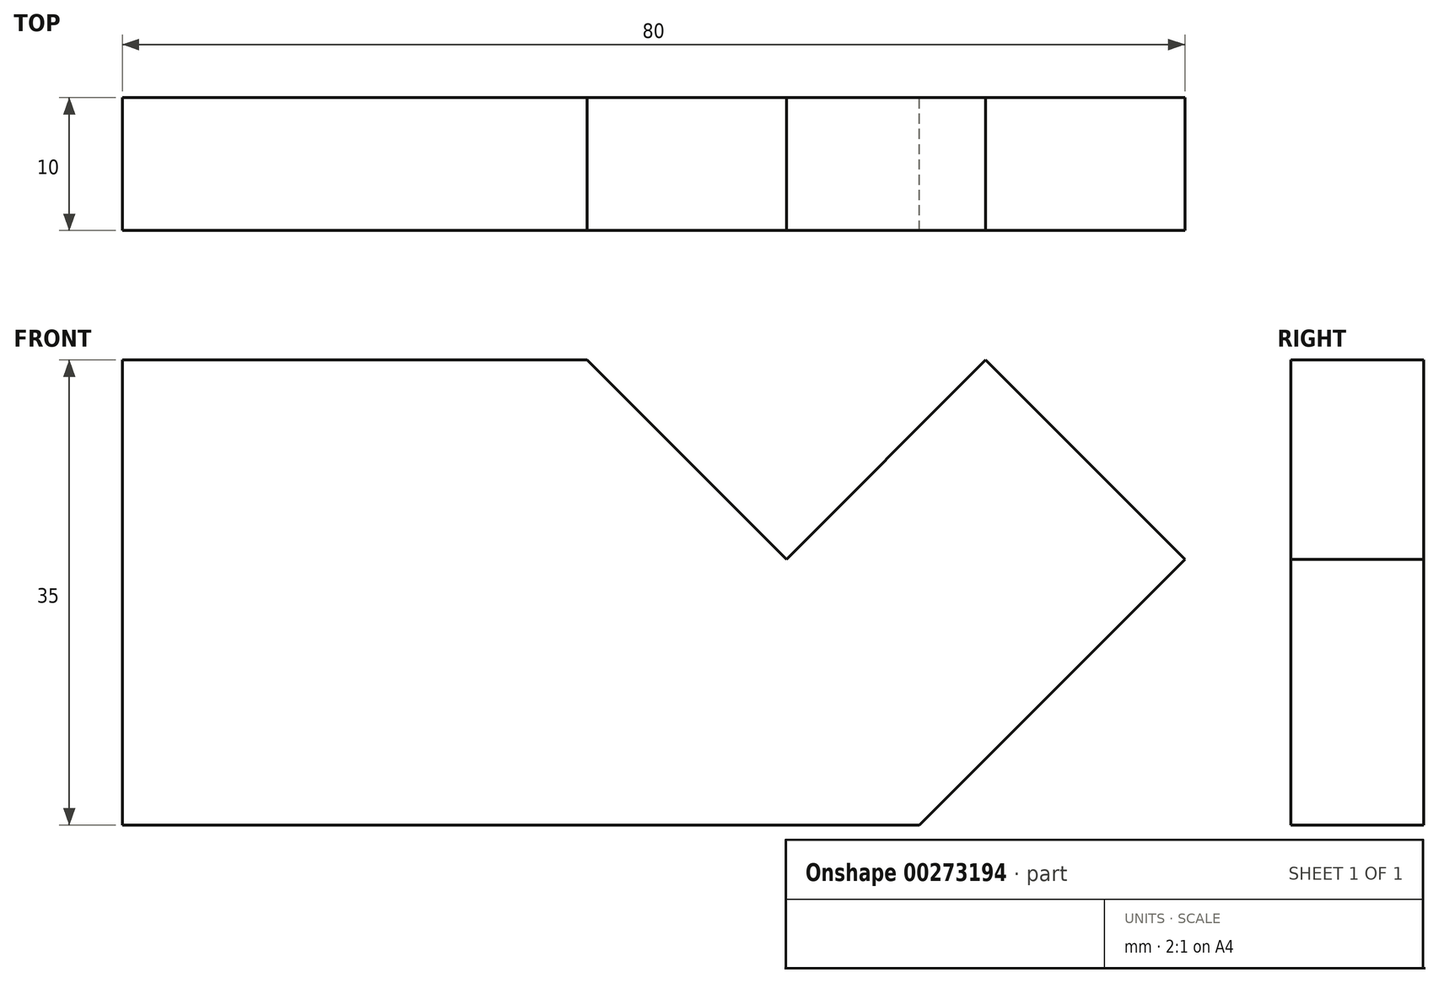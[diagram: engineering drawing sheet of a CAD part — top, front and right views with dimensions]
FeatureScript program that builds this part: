
annotation { "Feature Type Name" : "Feature", "Feature Type Description" : "" }
export const myFeature = defineFeature(function(context is Context, id is Id, definition is map)
    precondition{}
    {
        {
            var Q0;
            Q0=qCreatedBy(makeId("Front.planeOp"),FACE);
            var sketch = newSketch(context, id + "F0", { "sketchPlane" : qUnion([Q0])});
            skLineSegment(sketch, "E0", {"start": v(0, 0) * mm, "end": v(0, 35) * mm});
            skLineSegment(sketch, "E1", {"start": v(50, 20) * mm, "end": v(35, 35) * mm});
            skLineSegment(sketch, "E2", {"start": v(50, 20) * mm, "end": v(65, 35) * mm});
            skLineSegment(sketch, "E3", {"start": v(35, 35) * mm, "end": v(0, 35) * mm});
            skLineSegment(sketch, "E4", {"start": v(60, 0) * mm, "end": v(80, 20) * mm});
            skLineSegment(sketch, "E5", {"start": v(65, 35) * mm, "end": v(80, 20) * mm});
            skLineSegment(sketch, "E6", {"start": v(60, 0) * mm, "end": v(0, 0) * mm});
            skSolve(sketch);
        }
        {
            var Q0;
            Q0=makeQuery(id+"F0.imprint","IMPRINT",FACE,{"disambiguationData":[TD([[makeQuery(id+"F0.imprint","IMPRINT",EDGE,{"derivedFrom":sQuery(id+"F0.wireOp",EDGE,"E0")}),-1.0]])]});
            extrude(context, id + "F1", {"entities" : qUnion([Q0]), "depth" : 10 * mm});
        }
    });
